# Revit family: Loudspeaker-with Subwoofer-QSC-KC12-Ground Stacked MAT ADDED
name_source: partatom
category: Communication Devices
units: mm (PartAtom-declared; Revit-internal decimal feet)

## family parameters
Cut with Voids When Loaded = No
Host = Face
Maintain Annotation Orientation = No
OmniClass Number = 23.85.10.11.14.14.14
OmniClass Title = Loudspeakers
Part Type = Normal
Room Calculation Point = No
Round Connector Dimension = Use Diameter
Shared = No

## types (4) — shared parameters
Apparent Load = 394 VA
Comms Conduit Diameter = 1"
Current Draw = 1.8
Default Elevation = 48 "
Depth = 17.91 "
Depth Label = 15.54 "
Description = Active 3-Way Column Loudspeaker with Subwoofer.
Feet Width = 1.63 "
Feet X Offset = 4.7 "
Feet Y Offset = 15.6 "
Frequency Range = 40 Hz - 20 kHz
Full Load Current = 2 A
Half Depth = 13.59 "
IQ Category = Loudspeaker
Length 1 = 2 "
Length 7 = -7.13 "
Load Classification = Other
Manufacturer = QSC
Manufacturer URL = www.qsc.com
MasterFormat = 0
Model = KC12
Number of Poles = 2
Pivot to Front = 4.31 "
Power Conduit Diameter = 1"
Power Factor = 0.95
Product Documentation Link = https://www.qscaudio.com
Product Page URL = http://qscaudio.com
Regulatory Compliance = CE, WEEE, UL, China RoHS, RoHS II, FCC Class B
Rotation = 0.00°
SPL Max = 132
SPL Measurement Bandwidth = 1 W / 1 m
Speaker Height = 21.5 "
Subwoofer Depth = 17.91 "
Subwoofer Height = 25.79 "
Subwoofer Width = 14.02 "
Sustainability Rating = 0
Voltage = 208 V
Voltage AC = 100-240 VAC
Width = 14.02 "
zero-valued in all types: Cost MSRP, Cost Project, Power Active, Power Peak, Power Standby

## per-type parameters (varying)
| type | Body Material | Grille Material | Height | Pivot Z Offset | URL | Weight | Weight Product |
| KC12 Speaker - Black - 89.4" H | Paint - QSC - Black | Metal - QSC - Mesh 2 Black | 89.4 " | 79.2 " | www.qsc.com | 27.30 lbm | 27.3 |
| KC12 Speaker - White - 89.4" H | Paint - QSC - White | Fabric - QSC - White Mesh | 89.4 " | 79.2 " | www.qsc.com | 27.30 lbm | 27.3 |
| KC12 Speaker - White - 57.6" H | Paint - QSC - White | Fabric - QSC - White Mesh | 57.6 " | 47.4 " | www.qsc.com | 26.00 lbm | 26 |
| KC12 Speaker - Black - 57.6" H | Paint - QSC - Black | Metal - QSC - Mesh 2 Black | 57.6 " | 47.4 " | www.qsys.com | 26.00 lbm | 26 |

note: column(s) folded — value = type name in every type: Type Comments

## geometry (parser evidence)
native form markers: Sweep x5
no freeform markers — native parametric forms only
